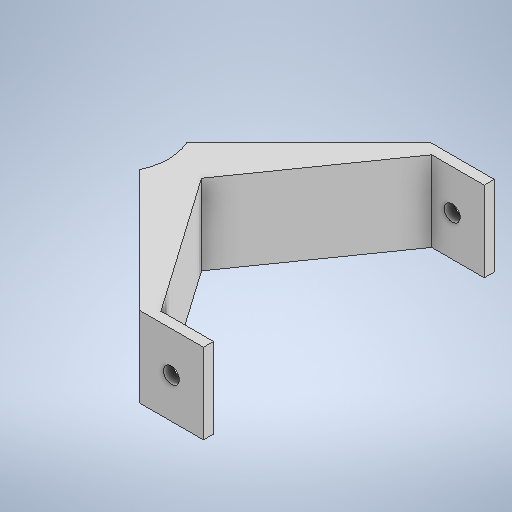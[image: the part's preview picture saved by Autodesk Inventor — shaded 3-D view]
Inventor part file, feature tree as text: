
AUTODESK INVENTOR PART (.ipt)
format: ipt  version: 2025.1 (Build 291241000, 241)  size: 252,416 bytes
history: native  units: in
note: dims shown in document units (in); Inventor stores cm internally (conversion verified against a paired STEP export)
features: extrude x2, sketch x2
ambient origin geometry x8: Origin, YZ Plane, XZ Plane, XY Plane, X Axis, Y Axis, Z Axis, Center Point
bodies: Solid1 (feature_tree)
feature tree (4):
  extrude  "Extrusion1"  TaperAngle=0.0deg  [1 undecoded]
  extrude  "Extrusion2"  Depth=3.625in
  sketch  "Sketch1"  dims[d1=0.8in d6=0.0in]
  sketch  "Sketch2"  dims[d17=1.0in d18=0.0in d19=0.4in d20=0.2in d21=5.625in d22=0.0in d26=1.0in d27=45.0deg d29=45.0deg d31=0.3779in d34=3.625in d23=0.0in d24=0.0in d25=0.0in]
note: 1 required parameter value undecoded (feature->parameter linkage not recoverable at this tier; creation-order binding heuristic only, values carry confidence <= 0.55)
